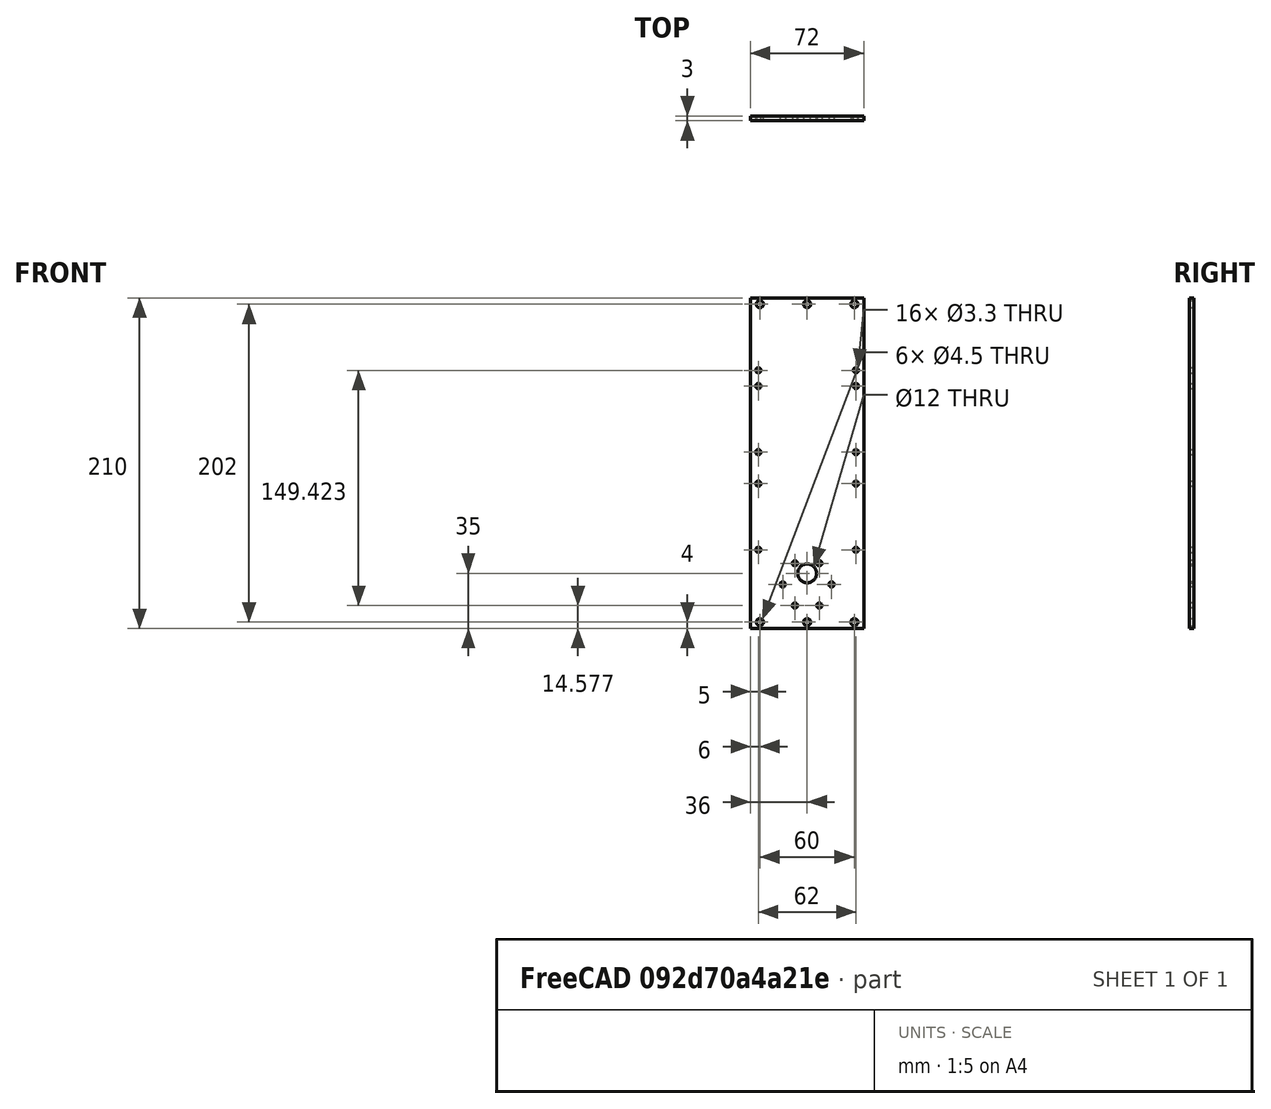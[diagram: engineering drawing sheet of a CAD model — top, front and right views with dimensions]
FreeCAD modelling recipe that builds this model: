
FCSTD DOCUMENT  (FreeCAD 0.17R13522 (Git))
Label: Seitenblech
License: All rights reserved
LicenseURL: http://en.wikipedia.org/wiki/All_rights_reserved
objects: TechDraw::DrawViewDimension×21, Sketcher::SketchObject×5, TechDraw::DrawViewAnnotation×4, PartDesign::Hole×3, TechDraw::DrawSVGTemplate×2, TechDraw::DrawProjGroupItem×2, TechDraw::DrawProjGroup×2, TechDraw::DrawPage×2, Part::Box×1, Part::Extrusion×1, Part::Mirroring×1, Part::Fuse×1, Part::Cut×1, PartDesign::FeatureBase×1, PartDesign::Body×1
note: 18 computed .brp shape members not serialized (recipe doc carries the construction recipe); baked Part::Feature solids carry a one-line shape summary decoded from their .brp

FEATURE [Part::Box] Box  label="Würfel"
  AttacherType = Attacher::AttachEngine3D
  Height = 210
  Length = 72
  Width = 3
FEATURE [Sketcher::SketchObject] Sketch
  MapMode = 5
  Placement = pos=(0,3,0) rot=(0,0.707107,0.707107;3.14159rad)
  Support = -> [Box]
  sketch-geometry (3):
    g0: Circle CenterX=-6 CenterY=4 CenterZ=0 NormalX=0 NormalY=0 NormalZ=1 AngleXU=0 Radius=2.25
    g1: Circle CenterX=-66 CenterY=4 CenterZ=0 NormalX=0 NormalY=0 NormalZ=1 AngleXU=0 Radius=2.25
    g2: Circle CenterX=-36 CenterY=4 CenterZ=0 NormalX=0 NormalY=0 NormalZ=1 AngleXU=0 Radius=2.25
  constraints (9):
    c: Radius(g0) = 2.25
    c: Radius(g2) = 2.25
    c: Radius(g1) = 2.25
    c: DistanceX(g0,g-1) = 6
    c: DistanceX(g2,g-1) = 36
    c: DistanceY(g0) = 4
    c: Horizontal(g0,g2)
    c: Horizontal(g2,g1)
    c: DistanceX(g1,g-1) = 66
FEATURE [Part::Extrusion] Extrude
  Base = -> Sketch
  Dir = (0,-4,0)
  DirMode = 0
  FaceMakerClass = Part::FaceMakerBullseye
  LengthFwd = 10
  LengthRev = 0
  Solid = true
  Symmetric = false
FEATURE [Part::Mirroring] Part__Mirroring  label="Extrude (Mirror #1)"
  Base = (0,0,105)
  Normal = (0,0,1)
  Source = -> Extrude
FEATURE [Part::Fuse] Fusion
  Base = -> Extrude
  Tool = -> Part__Mirroring
FEATURE [Part::Cut] Cut
  Base = -> Box
  Tool = -> Fusion
FEATURE [PartDesign::FeatureBase] BaseFeature
  BaseFeature = -> Cut
FEATURE [Sketcher::SketchObject] Sketch001
  MapMode = 5
  Placement = pos=(0,0,0) rot=(1,0,0;1.5708rad)
  Support = -> [BaseFeature]
  sketch-geometry (10):
    g0: Circle CenterX=67 CenterY=50 CenterZ=0 NormalX=0 NormalY=0 NormalZ=1 AngleXU=0 Radius=2.5
    g1: Circle CenterX=5 CenterY=50 CenterZ=0 NormalX=0 NormalY=0 NormalZ=1 AngleXU=0 Radius=2.5
    g2: Circle CenterX=67 CenterY=92 CenterZ=0 NormalX=0 NormalY=0 NormalZ=1 AngleXU=0 Radius=2.5
    g3: Circle CenterX=5 CenterY=92 CenterZ=0 NormalX=0 NormalY=0 NormalZ=1 AngleXU=0 Radius=2.5
    g4: Circle CenterX=67 CenterY=154 CenterZ=0 NormalX=0 NormalY=0 NormalZ=1 AngleXU=0 Radius=2.5
    g5: Circle CenterX=5 CenterY=154 CenterZ=0 NormalX=0 NormalY=0 NormalZ=1 AngleXU=0 Radius=2.5
    g6: Circle CenterX=5 CenterY=112 CenterZ=0 NormalX=0 NormalY=0 NormalZ=1 AngleXU=0 Radius=2.5
    g7: Circle CenterX=67 CenterY=112 CenterZ=0 NormalX=0 NormalY=0 NormalZ=1 AngleXU=0 Radius=2.5
    g8: Circle CenterX=5 CenterY=164 CenterZ=0 NormalX=0 NormalY=0 NormalZ=1 AngleXU=0 Radius=2.5
    g9: Circle CenterX=67 CenterY=164 CenterZ=0 NormalX=0 NormalY=0 NormalZ=1 AngleXU=0 Radius=2.5
  constraints (30):
    c: Radius(g0) = 2.5
    c: Radius(g1) = 2.5
    c: Radius(g3) = 2.5
    c: Radius(g2) = 2.5
    c: Radius(g4) = 2.5
    c: Radius(g5) = 2.5
    c: DistanceX(g-1,g1) = 5
    c: DistanceX(g-1,g0) = 67
    c: Vertical(g2,g0)
    c: Vertical(g4,g2)
    c: Vertical(g3,g1)
    c: Vertical(g5,g3)
    c: Horizontal(g5,g4)
    c: Horizontal(g3,g2)
    c: DistanceY(g-1,g1) = 50
    c: Horizontal(g1,g0)
    c: DistanceY(g1,g3) = 42
    c: DistanceY(g3,g5) = 62
    c: Vertical(g3,g6)
    c: Vertical(g8,g6)
    c: Vertical(g7,g9)
    c: Vertical(g7,g2)
    c: Horizontal(g6,g7)
    c: Horizontal(g9,g8)
    c: Radius(g8) = 2.5
    c: Radius(g9) = 2.5
    c: Radius(g7) = 2.5
    c: Radius(g6) = 2.5
    c: DistanceY(g1,g6) = 62
    c: DistanceY(g6,g8) = 52
FEATURE [PartDesign::Hole] Hole
  BaseFeature = -> BaseFeature
  Depth = 25
  DepthType = 0
  Diameter = 3.3
  DrillPoint = 1
  DrillPointAngle = 118
  HoleCutCountersinkAngle = 90
  HoleCutDepth = 0
  HoleCutDiameter = 3
  HoleCutType = 0
  ModelActualThread = false
  Profile = -> Sketch001
  Tapered = false
  TaperedAngle = 90
  ThreadAngle = 0
  ThreadClass = 0
  ThreadCutOffInner = 0
  ThreadCutOffOuter = 0
  ThreadDirection = 0
  ThreadFit = 0
  ThreadPitch = 0
  ThreadSize = 3
  ThreadType = 1
  Threaded = false
FEATURE [TechDraw::DrawSVGTemplate] Template
  EditableTexts = Designed_by_Name=Christian; FC-Date=24.05.2018; FC-SC=4/5; FC-SH=1/2; FC-Title=Kleinroboter2, Seitenblech; Subtitle=Bohrungen außen
  Height = 210
  Orientation = 1
  Width = 297
FEATURE [Sketcher::SketchObject] Sketch002
  MapMode = 5
  Placement = pos=(0,3,0) rot=(0,0.707107,0.707107;3.14159rad)
  Support = -> [Hole]
  sketch-geometry (9):
    g0: Circle CenterX=-36 CenterY=35 CenterZ=0 NormalX=0 NormalY=0 NormalZ=1 AngleXU=0 Radius=6
    g1: GeomPoint X=-36 Y=28 Z=0
    g2: GeomPoint X=-20.5 Y=28 Z=0
    g3: Circle CenterX=-20.5 CenterY=28 CenterZ=0 NormalX=0 NormalY=0 NormalZ=1 AngleXU=0 Radius=1.6
    g4: Circle CenterX=-28.25 CenterY=41.4234 CenterZ=0 NormalX=0 NormalY=0 NormalZ=1 AngleXU=0 Radius=1.6
    g5: Circle CenterX=-43.75 CenterY=41.4234 CenterZ=0 NormalX=0 NormalY=0 NormalZ=1 AngleXU=0 Radius=1.6
    g6: Circle CenterX=-43.75 CenterY=14.5766 CenterZ=0 NormalX=0 NormalY=0 NormalZ=1 AngleXU=0 Radius=1.6
    g7: Circle CenterX=-28.25 CenterY=14.5766 CenterZ=0 NormalX=0 NormalY=0 NormalZ=1 AngleXU=0 Radius=1.6
    g8: Circle CenterX=-51.5 CenterY=28 CenterZ=0 NormalX=0 NormalY=0 NormalZ=1 AngleXU=0 Radius=1.6
  constraints (24):
    c: Radius(g0) = 6
    c: DistanceY(g1,g0) = 7
    c: Vertical(g1,g0)
    c: DistanceX(g1,g-1) = 36
    c: Coincident(g3,g2)
    c: Radius(g6) = 1.6
    c: Radius(g8) = 1.6
    c: Radius(g7) = 1.6
    c: Radius(g3) = 1.6
    c: Radius(g4) = 1.6
    c: Radius(g5) = 1.6
    c: DistanceY(g-1,g1) = 28
    c: Distance(g2,g1) = 15.5
    c: Distance(g7,g2) = 15.5
    c: Distance(g2,g4) = 15.5
    c: Distance(g4,g5) = 15.5
    c: Distance(g8,g5) = 15.5
    c: Distance(g8,g6) = 15.5
    c: Distance(g6,g7) = 15.5
    c: Horizontal(g8,g2)
    c: Horizontal(g6,g7)
    c: Vertical(g5,g6)
    c: DistanceX(g8,g1) = 15.5
    c: Horizontal(g1,g2)
FEATURE [PartDesign::Hole] Hole001
  BaseFeature = -> Hole
  Depth = 25
  DepthType = 1
  Diameter = 3.3
  DrillPoint = 1
  DrillPointAngle = 118
  HoleCutCountersinkAngle = 90
  HoleCutDepth = 0
  HoleCutDiameter = 3
  HoleCutType = 0
  ModelActualThread = false
  Profile = -> Sketch002
  Tapered = false
  TaperedAngle = 90
  ThreadAngle = 60
  ThreadClass = 0
  ThreadCutOffInner = 0.0541266
  ThreadCutOffOuter = 0.108253
  ThreadDirection = 0
  ThreadFit = 0
  ThreadPitch = 0.5
  ThreadSize = 3
  ThreadType = 1
  Threaded = false
FEATURE [Sketcher::SketchObject] Sketch003
  MapMode = 5
  Placement = pos=(0,3,0) rot=(0,0.707107,0.707107;3.14159rad)
  Support = -> [Hole]
  sketch-geometry (16):
    g0: Circle CenterX=-36 CenterY=35 CenterZ=0 NormalX=0 NormalY=0 NormalZ=1 AngleXU=0 Radius=6
    g1: GeomPoint X=-36 Y=28 Z=0
    g2: GeomPoint X=-20 Y=28 Z=0
    g3: LineSegment StartX=-20 StartY=28 StartZ=0 EndX=-28 EndY=41.8564 EndZ=0
    g4: LineSegment StartX=-28 StartY=41.8564 StartZ=0 EndX=-44 EndY=41.8564 EndZ=0
    g5: LineSegment StartX=-44 StartY=41.8564 StartZ=0 EndX=-52 EndY=28 EndZ=0
    g6: LineSegment StartX=-52 StartY=28 StartZ=0 EndX=-44 EndY=14.1436 EndZ=0
    g7: LineSegment StartX=-44 StartY=14.1436 StartZ=0 EndX=-28 EndY=14.1436 EndZ=0
    g8: LineSegment StartX=-28 StartY=14.1436 StartZ=0 EndX=-20 EndY=28 EndZ=0
    g9: Circle [constr] CenterX=-36 CenterY=28 CenterZ=0 NormalX=0 NormalY=0 NormalZ=1 AngleXU=0 Radius=16
    g10: Circle CenterX=-20 CenterY=28 CenterZ=0 NormalX=0 NormalY=0 NormalZ=1 AngleXU=0 Radius=1.6
    g11: Circle CenterX=-28 CenterY=41.8564 CenterZ=0 NormalX=0 NormalY=0 NormalZ=1 AngleXU=0 Radius=1.6
    g12: Circle CenterX=-44 CenterY=41.8564 CenterZ=0 NormalX=0 NormalY=0 NormalZ=1 AngleXU=0 Radius=1.6
    g13: Circle CenterX=-44 CenterY=14.1436 CenterZ=0 NormalX=0 NormalY=0 NormalZ=1 AngleXU=0 Radius=1.6
    g14: Circle CenterX=-28 CenterY=14.1436 CenterZ=0 NormalX=0 NormalY=0 NormalZ=1 AngleXU=0 Radius=1.6
    g15: Circle CenterX=-52 CenterY=28 CenterZ=0 NormalX=0 NormalY=0 NormalZ=1 AngleXU=0 Radius=1.6
  constraints (34):
    c: Radius(g0) = 6
    c: DistanceY(g-1,g0) = 35
    c: DistanceX(g0,g-1) = 36
    c: Vertical(g1,g0)
    c: DistanceY(g1,g0) = 7
    c: Horizontal(g2,g1)
    c: DistanceX(g1,g2) = 16
    c: Coincident(g3,g4)
    c: Coincident(g4,g5)
    c: Coincident(g5,g6)
    c: Coincident(g6,g7)
    c: Coincident(g7,g8)
    c: Coincident(g8,g3)
    c: Equal(g3, g4-g8) x5
    c: PointOnObject(g3,g9)
    c: PointOnObject(g4,g9)
    c: PointOnObject(g5,g9)
    c: PointOnObject(g6,g9)
    c: PointOnObject(g7,g9)
    c: PointOnObject(g8,g9)
    c: Coincident(g9,g1)
    c: Coincident(g8,g2)
    c: Coincident(g10,g2)
    c: Coincident(g11,g3)
    c: Coincident(g12,g4)
    c: Coincident(g13,g6)
    c: Coincident(g14,g7)
    c: Coincident(g15,g5)
    c: Radius(g10) = 1.6
    c: Radius(g11) = 1.6
    c: Radius(g12) = 1.6
    c: Radius(g15) = 1.6
    c: Radius(g13) = 1.6
    c: Radius(g14) = 1.6
FEATURE [Sketcher::SketchObject] Sketch004
  MapMode = 5
  Placement = pos=(0,0,0) rot=(1,0,0;1.5708rad)
  Support = -> [Hole001]
  sketch-geometry (2):
    g0: GeomPoint X=36 Y=35 Z=0
    g1: Circle CenterX=36 CenterY=35 CenterZ=0 NormalX=0 NormalY=0 NormalZ=1 AngleXU=0 Radius=6.1
  constraints (4):
    c: DistanceX(g-1,g0) = 36
    c: DistanceY(g-1,g0) = 35
    c: Coincident(g1,g0)
    c: Radius(g1) = 6.1
FEATURE [PartDesign::Hole] Hole002
  BaseFeature = -> Hole001
  Depth = 25
  DepthType = 0
  Diameter = 12
  DrillPoint = 1
  DrillPointAngle = 118
  HoleCutCountersinkAngle = 90
  HoleCutDepth = 0
  HoleCutDiameter = 0
  HoleCutType = 0
  ModelActualThread = false
  Profile = -> Sketch004
  Tapered = false
  TaperedAngle = 90
  ThreadAngle = 0
  ThreadClass = 0
  ThreadCutOffInner = 0
  ThreadCutOffOuter = 0
  ThreadDirection = 0
  ThreadFit = 0
  ThreadPitch = 0
  ThreadSize = 0
  ThreadType = 0
  Threaded = false
FEATURE [PartDesign::Body] Body
  BaseFeature = -> Cut
  Group = -> [BaseFeature,Sketch001,Hole,Sketch002,Hole001,Sketch004,Hole002]
  Origin = -> Origin
  Tip = -> Hole002
FEATURE [TechDraw::DrawProjGroupItem] ProjItem
  CoarseView = false
  Direction = (0,1,0)
  Focus = 100
  HardHidden = false
  IsoCount = 0
  IsoHidden = false
  IsoVisible = false
  LockPosition = true
  Perspective = false
  Rotation = 0
  RotationVector = (0,0,-1)
  ScaleType = 0
  SeamHidden = false
  SeamVisible = false
  SmoothHidden = false
  SmoothVisible = false
  Source = -> [Body]
  Type = 0
  X = 0
  Y = 0
FEATURE [TechDraw::DrawProjGroup] ProjGroup
  Anchor = -> ProjItem
  AutoDistribute = true
  CubeDirs = (6) [(1,3.67394e-16,6.12323e-17),(-3.67394e-16,1,-2.46519e-32),(-6.12323e-17,2.15551e-33,1),(3.67394e-16,-1,2.46519e-32),(6.12323e-17,-2.15551e-33,-1),+1 more]
  CubeRotations = (6) [(-6.12323e-17,2.15551e-33,-1),(-6.12323e-17,2.15551e-33,-1),(-3.67394e-16,-1,-2.03409e-32),(6.12323e-17,-2.15551e-33,1),(3.67394e-16,1,2.03409e-32),+1 more]
  LockPosition = false
  ProjectionType = 0
  Rotation = 0
  Scale = 0.8
  ScaleType = 2
  Source = -> [Body]
  Views = -> [ProjItem]
  X = 109.889
  Y = 156.539
  spacingX = 15
  spacingY = 15
FEATURE [TechDraw::DrawViewDimension] Dimension013
  FormatSpec = %.2f
  LockPosition = false
  MeasureType = 1
  References2D = -> [ProjItem]
  Rotation = 0
  ScaleType = 0
  Type = 1
  X = 11.1735
  Y = -93.3367
FEATURE [TechDraw::DrawSVGTemplate] Template001
  EditableTexts = Designed_by_Name=Christian Dengler; FC-Date=24.05.2018; FC-SC=1/1; FC-SH=2/2; FC-Title=Kleinroboter2, Seitenblech; Subtitle=Bemaßungen, Motoranbringung
  Height = 210
  Orientation = 1
  Width = 297
FEATURE [TechDraw::DrawProjGroupItem] ProjItem001
  CoarseView = false
  Direction = (0,-1,0)
  Focus = 100
  HardHidden = false
  IsoCount = 0
  IsoHidden = false
  IsoVisible = false
  LockPosition = false
  Perspective = false
  Rotation = 0
  RotationVector = (0,0,-1)
  ScaleType = 0
  SeamHidden = false
  SeamVisible = false
  SmoothHidden = false
  SmoothVisible = false
  Source = -> [Body]
  Type = 0
  X = 0
  Y = 0
FEATURE [TechDraw::DrawProjGroup] ProjGroup001
  Anchor = -> ProjItem001
  AutoDistribute = true
  CubeDirs = (6) [(-1,0,-6.12323e-17),(0,-1,0),(-6.12323e-17,0,1),(0,1,0),(6.12323e-17,0,-1),(1,0,6.12323e-17)]
  CubeRotations = (6) [(-6.12323e-17,0,-1),(-6.12323e-17,0,-1),(0,1,0),(6.12323e-17,0,1),(0,-1,0),(-6.12323e-17,0,-1)]
  LockPosition = false
  ProjectionType = 0
  Rotation = 0
  ScaleType = 0
  Source = -> [Body]
  Views = -> [ProjItem001]
  X = 121.528
  Y = 144.567
  spacingX = 15
  spacingY = 15
FEATURE [TechDraw::DrawViewAnnotation] Annotation
  Font = osifont
  LineSpace = 80
  LockPosition = false
  MaxWidth = -1
  Rotation = 0
  ScaleType = 0
  Text = Blechdicke 3mm
  TextSize = 8
  TextStyle = 0
  X = 69.3073
  Y = 51.7774
FEATURE [TechDraw::DrawViewAnnotation] Annotation001
  Font = osifont
  LineSpace = 80
  LockPosition = false
  MaxWidth = -1
  Rotation = 0
  ScaleType = 0
  Text = Blechdicke 3mm 
  TextSize = 8
  TextStyle = 0
  X = 73.8351
  Y = 37.0586
FEATURE [TechDraw::DrawViewDimension] Dimension040
  FormatSpec = %.2f
  LockPosition = false
  MeasureType = 1
  References2D = -> [ProjItem]
  Rotation = 0
  ScaleType = 0
  Type = 2
  X = 160.668
  Y = -17.5498
FEATURE [TechDraw::DrawViewDimension] Dimension064
  FormatSpec = %.2f
  LockPosition = false
  MeasureType = 1
  References2D = -> [ProjItem001]
  Rotation = 0
  ScaleType = 0
  Type = 1
  X = 92.8276
  Y = -54.0552
FEATURE [TechDraw::DrawViewDimension] Dimension066
  FormatSpec = %.2f
  LockPosition = false
  MeasureType = 1
  References2D = -> [ProjItem001]
  Rotation = 0
  ScaleType = 0
  Type = 5
  X = 38.1172
  Y = 44.2352
FEATURE [TechDraw::DrawViewDimension] Dimension072
  FormatSpec = %.2f
  LockPosition = false
  MeasureType = 1
  References2D = -> [ProjItem001]
  Rotation = 0
  ScaleType = 0
  Type = 2
  X = 29.2314
  Y = 0
FEATURE [TechDraw::DrawViewDimension] Dimension073
  FormatSpec = %.2f
  LockPosition = false
  MeasureType = 1
  References2D = -> [ProjItem001]
  Rotation = 0
  ScaleType = 0
  Type = 2
  X = 127.527
  Y = -20.1065
FEATURE [TechDraw::DrawViewDimension] Dimension074
  FormatSpec = %.2f
  LockPosition = false
  MeasureType = 1
  References2D = -> [ProjItem001]
  Rotation = 0
  ScaleType = 0
  Type = 1
  X = 89.3621
  Y = -67.2077
FEATURE [TechDraw::DrawViewDimension] Dimension075
  FormatSpec = %.2f
  LockPosition = false
  MeasureType = 1
  References2D = -> [ProjItem001]
  Rotation = 0
  ScaleType = 0
  Type = 5
  X = -1.0197
  Y = 46.4984
FEATURE [TechDraw::DrawViewAnnotation] Annotation002
  Font = osifont
  LineSpace = 80
  LockPosition = false
  MaxWidth = -1
  Rotation = 0
  ScaleType = 0
  Text = h7
  TextSize = 4
  TextStyle = 0
  X = 122.069
  Y = 187.522
FEATURE [TechDraw::DrawViewAnnotation] Annotation003
  Font = osifont
  LineSpace = 80
  LockPosition = false
  MaxWidth = -1
  Rotation = 0
  ScaleType = 0
  Text = Gleichmäßiges Hexagon (6*60° |  31mm Durchmesser)
  TextSize = 3
  TextStyle = 0
  X = 119.602
  Y = 148.346
FEATURE [TechDraw::DrawPage] Page003  label="Page2"
  KeepUpdated = true
  ProjectionType = 0
  Template = -> Template001
  Views = -> [ProjGroup001,Annotation,Dimension064,Dimension066,Dimension072,Dimension073,Dimension074,Dimension075,Annotation002,Annotation003]
FEATURE [TechDraw::DrawViewDimension] Dimension078
  FormatSpec = %.2f
  LockPosition = false
  MeasureType = 1
  References2D = -> [ProjItem]
  Rotation = 0
  ScaleType = 0
  Type = 5
  X = 44.9545
  Y = 38.5006
FEATURE [TechDraw::DrawViewDimension] Dimension079
  FormatSpec = %.2f
  LockPosition = false
  MeasureType = 1
  References2D = -> [ProjItem]
  Rotation = 0
  ScaleType = 0
  Type = 5
  X = -16.9136
  Y = 36.2751
FEATURE [TechDraw::DrawViewDimension] Dimension080
  FormatSpec = %.2f
  LockPosition = false
  MeasureType = 1
  References2D = -> [ProjItem]
  Rotation = 0
  ScaleType = 0
  Type = 1
  X = 66.764
  Y = -34.0497
FEATURE [TechDraw::DrawViewDimension] Dimension081
  FormatSpec = %.2f
  LockPosition = false
  MeasureType = 1
  References2D = -> [ProjItem]
  Rotation = 0
  ScaleType = 0
  Type = 2
  X = 111.496
  Y = -53.4112
FEATURE [TechDraw::DrawViewDimension] Dimension
  FormatSpec = %.2f
  LockPosition = false
  MeasureType = 1
  References2D = -> [ProjItem]
  Rotation = 0
  ScaleType = 0
  Type = 2
  X = 123.959
  Y = -53.6338
FEATURE [TechDraw::DrawViewDimension] Dimension082
  FormatSpec = %.2f
  LockPosition = false
  MeasureType = 1
  References2D = -> [ProjItem]
  Rotation = 0
  ScaleType = 0
  Type = 2
  X = 141.095
  Y = -16.0234
FEATURE [TechDraw::DrawViewDimension] Dimension083
  FormatSpec = %.2f
  LockPosition = false
  MeasureType = 1
  References2D = -> [ProjItem]
  Rotation = 0
  ScaleType = 0
  Type = 2
  X = 151.332
  Y = -16.2459
FEATURE [TechDraw::DrawViewDimension] Dimension084
  FormatSpec = %.2f
  LockPosition = false
  MeasureType = 1
  References2D = -> [ProjItem]
  Rotation = 0
  ScaleType = 0
  Type = 1
  X = 65.8739
  Y = -40.7261
FEATURE [TechDraw::DrawViewDimension] Dimension085
  FormatSpec = %.2f
  LockPosition = false
  MeasureType = 1
  References2D = -> [ProjItem]
  Rotation = 0
  ScaleType = 0
  Type = 1
  X = 66.0964
  Y = -48.9603
FEATURE [TechDraw::DrawViewDimension] Dimension086
  FormatSpec = %.2f
  LockPosition = false
  MeasureType = 1
  References2D = -> [ProjItem]
  Rotation = 0
  ScaleType = 0
  Type = 1
  X = 43.6192
  Y = -56.972
FEATURE [TechDraw::DrawViewDimension] Dimension087
  FormatSpec = %.2f
  LockPosition = false
  MeasureType = 1
  References2D = -> [ProjItem]
  Rotation = 0
  ScaleType = 0
  Type = 1
  X = 28.7085
  Y = -65.8739
FEATURE [TechDraw::DrawViewDimension] Dimension088
  FormatSpec = %.2f
  LockPosition = false
  MeasureType = 1
  References2D = -> [ProjItem]
  Rotation = 0
  ScaleType = 0
  Type = 1
  X = 20.2518
  Y = -77.2237
FEATURE [TechDraw::DrawViewDimension] Dimension089
  FormatSpec = %.2f
  LockPosition = false
  MeasureType = 1
  References2D = -> [ProjItem]
  Rotation = 0
  ScaleType = 0
  Type = 1
  X = 16.4685
  Y = -85.6805
FEATURE [TechDraw::DrawPage] Page
  KeepUpdated = true
  ProjectionType = 0
  Template = -> Template
  Views = -> [ProjGroup,Dimension013,Annotation001,Dimension040,Dimension078,Dimension079,Dimension080,Dimension081,Dimension,Dimension082,Dimension083,Dimension084,Dimension085,Dimension086,Dimension087,Dimension088,Dimension089]
